# Revit family: AD-S8T - Yoke Mount
name_source: partatom
category: Communication Devices
revit_build: Autodesk Revit Architecture 2012 (Build: 20110309_2315(x64)
units: mm (PartAtom-declared; Revit-internal decimal feet)

## types (1)
- AD-S8T - Yoke Mount
    100V Taps = 60, 30, 15
    70V Taps = 60, 30, 15, 7.5
    Coverage Horizontal = 105.00°
    Coverage Vertical = 105.00°
    Default Elevation = 0 mm  [stored 0 ft]
    Depth = 254 mm
    Description = 8" 2-Way Surface Mount Loudspeaker
    Height = 440 mm  [stored 1.44357 ft]
    Impedance = 8
    Manufacturer = QSC Audio Products, LLC
    Manufacturer URL = www.qscaudio.com
    Model = AD-S8T
    Mount Depth = 215 mm  [stored 0.705381 ft]
    Mount Height = 445 mm  [stored 1.45997 ft]
    Mount Width = 115 mm  [stored 0.377297 ft]
    Power Handling = 200
    Product Documentation Link = TBA
    Product Page URL = TBA
    Regulatory Compliance = RoHS
    SPL Max = 119
    Sensitivity = 90
    URL = TBA
    Weight Dimensional (kg) = 14.5
    Weight Dimensional (lb) = 32.1
    Weight Product (kg) = 11
    Weight Product (lb) = 24.1
    Width = 254 mm

note: [stored X ft] marks values corroborated as IEEE doubles in the binary element streams (Revit-internal decimal feet)

## geometry (parser evidence)
native form markers: Blend x1, Sweep x3
no freeform markers — native parametric forms only
